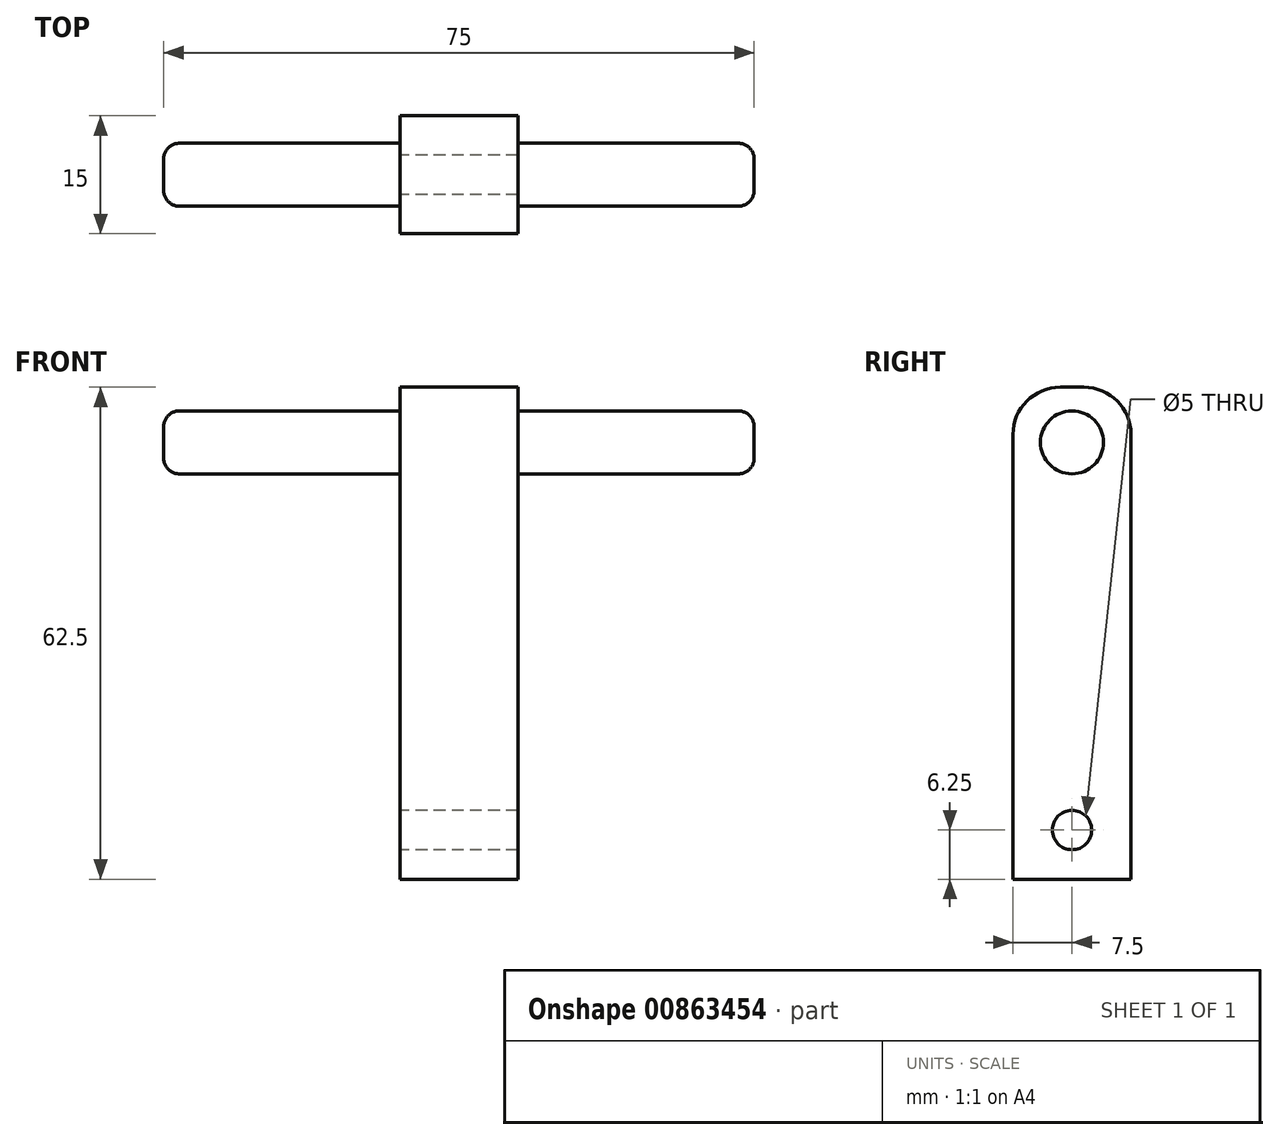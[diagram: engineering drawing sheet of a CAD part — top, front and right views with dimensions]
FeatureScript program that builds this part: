
annotation { "Feature Type Name" : "Feature", "Feature Type Description" : "" }
export const myFeature = defineFeature(function(context is Context, id is Id, definition is map)
    precondition{}
    {
        {
            var Q0;
            Q0=qCreatedBy(makeId("Top.planeOp"),FACE);
            var sketch = newSketch(context, id + "F0", { "sketchPlane" : qUnion([Q0])});
            skLineSegment(sketch, "E0.bottom", {"start": v(7.5, -7.5) * mm, "end": v(-7.5, -7.5) * mm});
            skLineSegment(sketch, "E0.top", {"start": v(7.5, 7.5) * mm, "end": v(-7.5, 7.5) * mm});
            skLineSegment(sketch, "E0.left", {"start": v(7.5, -7.5) * mm, "end": v(7.5, 7.5) * mm});
            skLineSegment(sketch, "E0.right", {"start": v(-7.5, -7.5) * mm, "end": v(-7.5, 7.5) * mm});
            skPoint(sketch, "E0.middle", {"position": v(0, 0) * mm});
            skSolve(sketch);
        }
        {
            var Q0;
            Q0=makeQuery(id+"F0.imprint","IMPRINT",FACE,{"disambiguationData":[TD([[makeQuery(id+"F0.imprint","IMPRINT",EDGE,{"derivedFrom":sQuery(id+"F0.wireOp",EDGE,"E0.bottom")}),-1.0]])]});
            extrude(context, id + "F1", {"entities" : qUnion([Q0]), "depth" : 62.5 * mm, "offsetDistance" : 25 * mm});
        }
        {
            var Q0;
            Q0=makeQuery(id+"F1.opExtrude","SWEPT_FACE",FACE,{"disambiguationData":[OSD([sQuery(id+"F0.wireOp",EDGE,"E0.left")])]});
            var sketch = newSketch(context, id + "F2", { "sketchPlane" : qUnion([Q0])});
            skCircle(sketch, "E1", {"center": v(0, 55.5) * mm, "radius": 4 * mm});
            skPoint(sketch, "E1.centerSnap0", {"position": v(0, 62.5) * mm});
            skSolve(sketch);
        }
        {
            var Q0;
            Q0=makeQuery(id+"F1.opExtrude","CAP_EDGE",EDGE,{"disambiguationData":[OSD([sQuery(id+"F0.wireOp",EDGE,"E0.bottom")])],"isStart":false});
            fillet(context, id + "F3", {"entities" : qUnion([Q0]), "radius" : 6 * mm, "tangentPropagation" : true, "allowEdgeOverflow" : false});
        }
        {
            var Q0;
            Q0=makeQuery(id+"F1.opExtrude","CAP_EDGE",EDGE,{"disambiguationData":[OSD([sQuery(id+"F0.wireOp",EDGE,"E0.top")])],"isStart":false});
            fillet(context, id + "F4", {"entities" : qUnion([Q0]), "radius" : 6 * mm, "tangentPropagation" : true, "allowEdgeOverflow" : false});
        }
        {
            var Q0;
            Q0=makeQuery(id+"F2.imprint","IMPRINT",FACE,{"disambiguationData":[TD([[makeQuery(id+"F2.imprint","IMPRINT",EDGE,{"derivedFrom":sQuery(id+"F2.wireOp",EDGE,"E1")}),1.0]])]});
            extrude(context, id + "F5", {"entities" : qUnion([Q0]), "operationType" : NewBodyOperationType.ADD, "depth" : 30 * mm, "offsetDistance" : 25 * mm});
        }
        {
            var Q0;
            Q0=makeQuery(id+"F1.opExtrude","SWEPT_FACE",FACE,{"disambiguationData":[OSD([sQuery(id+"F0.wireOp",EDGE,"E0.right")])]});
            var sketch = newSketch(context, id + "F6", { "sketchPlane" : qUnion([Q0])});
            skCircle(sketch, "E2", {"center": v(0, 55.5) * mm, "radius": 4 * mm});
            skPoint(sketch, "E2.centerSnap0", {"position": v(0, 62.5) * mm});
            skSolve(sketch);
        }
        {
            var Q0;
            Q0=makeQuery(id+"F6.imprint","IMPRINT",FACE,{"disambiguationData":[TD([[makeQuery(id+"F6.imprint","IMPRINT",EDGE,{"derivedFrom":sQuery(id+"F6.wireOp",EDGE,"E2")}),1.0]])]});
            extrude(context, id + "F7", {"entities" : qUnion([Q0]), "operationType" : NewBodyOperationType.ADD, "depth" : 30 * mm, "offsetDistance" : 25 * mm});
        }
        {
            var Q0;
            Q0=makeQuery(id+"F1.opExtrude","SWEPT_FACE",FACE,{"disambiguationData":[OSD([sQuery(id+"F0.wireOp",EDGE,"E0.right")])]});
            var sketch = newSketch(context, id + "F8", { "sketchPlane" : qUnion([Q0])});
            skCircle(sketch, "E3", {"center": v(0, 6.25) * mm, "radius": 2.5 * mm});
            skPoint(sketch, "E3.centerSnap0", {"position": v(0, 0) * mm});
            skSolve(sketch);
        }
        {
            var Q0;
            Q0=sQuery(id+"F8.wireOp",VERTEX,"E3.center");
            var Q1;
            Q1=makeQuery(id+"F1.opExtrude","SWEPT_BODY",BODY,{"disambiguationData":[OSD([sQuery(id+"F0.wireOp",EDGE,"E0.bottom"),sQuery(id+"F0.wireOp",EDGE,"E0.top"),sQuery(id+"F0.wireOp",EDGE,"E0.left"),sQuery(id+"F0.wireOp",EDGE,"E0.right")])]});
            hole(context, id + "F9", {"style" : HoleStyle.SIMPLE, "endStyle" : HoleEndStyle.THROUGH, "holeDiameter" : 5 * mm, "majorDiameter" : 5 * mm, "isTappedThrough" : true, "tappedDepth" : 12 * mm, "tapClearance" : 3, "locations" : qUnion([Q0]), "scope" : qUnion([Q1])});
        }
        {
            var Q0;
            Q0=makeQuery(id+"F7.opExtrude","CAP_EDGE",EDGE,{"disambiguationData":[OSD([sQuery(id+"F6.wireOp",EDGE,"E2")])],"isStart":false});
            fillet(context, id + "F10", {"entities" : qUnion([Q0]), "radius" : 2 * mm, "tangentPropagation" : true, "allowEdgeOverflow" : false});
        }
        {
            var Q0;
            Q0=makeQuery(id+"F5.opExtrude","CAP_EDGE",EDGE,{"disambiguationData":[OSD([sQuery(id+"F2.wireOp",EDGE,"E1")])],"isStart":false});
            fillet(context, id + "F11", {"entities" : qUnion([Q0]), "radius" : 2 * mm, "tangentPropagation" : true, "allowEdgeOverflow" : false});
        }
    });
